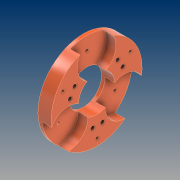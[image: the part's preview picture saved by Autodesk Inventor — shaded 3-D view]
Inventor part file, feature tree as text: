
AUTODESK INVENTOR PART (.ipt)
format: ipt  version: 2021 (Build 250183000, 183)  size: 325,120 bytes
history: native  units: mm
features: extrude x9, sketch x8, pattern_circular x8, thread x6, plane x3, revolve x1
ambient origin geometry x8: Origin, YZ Plane, XZ Plane, XY Plane, X Axis, Y Axis, Z Axis, Center Point
bodies: Body1 (feature_tree)
feature tree (35):
  sketch  "Sketch6"  dims[d21=235.0mm d22=30.0mm d24=360.0deg]
  extrude  "Extrusion4"  Depth=235.0mm TaperAngle=360.0deg
  extrude  "Extrusion5"  Depth=550.0mm
  extrude  "Extrusion6"  Depth=20.0mm
  extrude  "Extrusion7"  Depth=20.0mm
  extrude  "Extrusion8"  Depth=15.0mm TaperAngle=0.0deg
  extrude  "Extrusion9"  Depth=470.0mm
  extrude  "Extrusion10"  Depth=170.0mm
  pattern_circular  "Circular Pattern1"  Count=17  [1 undecoded]
  plane  "Work Plane1"
  plane  "Work Plane2"
  sketch  "Sketch14"  dims[d40=0.0mm d41=0.0mm d42=470.0mm]
  extrude  "Extrusion12"  Depth=196.0mm
  pattern_circular  "Circular Pattern5"  [2 undecoded]
  pattern_circular  "Circular Pattern7"  Count=22  [1 undecoded]
  plane  "Work Plane3"
  revolve  "Revolution4"  [1 undecoded]
  pattern_circular  "Circular Pattern8"  [2 undecoded]
  pattern_circular  "Circular Pattern9"  [2 undecoded]
  pattern_circular  "Circular Pattern10"  Count=6  [1 undecoded]
  pattern_circular  "Circular Pattern11"  Count=3 Angle=360.0deg
  thread  "Thread9"  [1 undecoded]
  thread  "Thread10"  [1 undecoded]
  thread  "Thread11"  [1 undecoded]
  thread  "Thread12"  [1 undecoded]
  thread  "Thread13"  [1 undecoded]
  thread  "Thread14"  [1 undecoded]
  extrude  "Extrusion14"  Depth=60.0mm TaperAngle=0.0deg
  pattern_circular  "Circular Pattern12"  Count=3 Angle=360.0deg
  sketch  "Sketch7"  dims[d26=195.0mm d27=550.0mm]
  sketch  "Sketch9"  dims[d28=20.0mm d29=0.0mm d30=550.0mm]
  sketch  "Sketch10"  dims[d31=60.0mm d32=0.0mm d33=20.0mm]
  sketch  "Sketch12"  dims[d34=30.0mm d36=360.0deg d38=15.0mm d39=0.0mm]
  sketch  "Sketch15"  dims[d44=20.0mm d48=25.0mm d50=170.0mm]
  sketch  "Sketch16"  dims[d55=0.0mm d56=0.0mm d58=196.0mm d60=294.0mm d61=220.0mm d62=0.0mm d63=0.0mm d64=25.0mm d65=3.490659mm d66=60.0mm d67=0.0mm d68=30.0mm d69=360.0deg d83=63.5mm d88=101.5mm d96=20.0mm d98=30.0mm d101=1.0mm d102=20.0mm d106=30.0mm d107=20.0mm d109=30.0mm d111=60.0mm d112=0.0mm d118=30.0mm d119=360.0deg d124=30.0mm d125=360.0deg d127=113.0mm d129=90.0deg d130=20.0mm d131=59.341195mm d133=30.0mm d134=360.0deg d136=30.0mm d137=360.0deg d139=30.0mm d140=360.0deg d150=126.987402mm d152=12.265489mm d154=12.5mm d155=60.0mm d156=0.0mm d157=60.0mm d158=0.0mm d159=60.0mm d160=0.0mm d161=60.0mm d162=0.0mm d163=60.0mm d164=0.0mm d165=60.0mm d166=0.0mm d167=0.0mm d168=0.0mm d169=30.0mm d170=360.0deg]
note: 16 required parameter values undecoded (feature->parameter linkage not recoverable at this tier; creation-order binding heuristic only, values carry confidence <= 0.55)